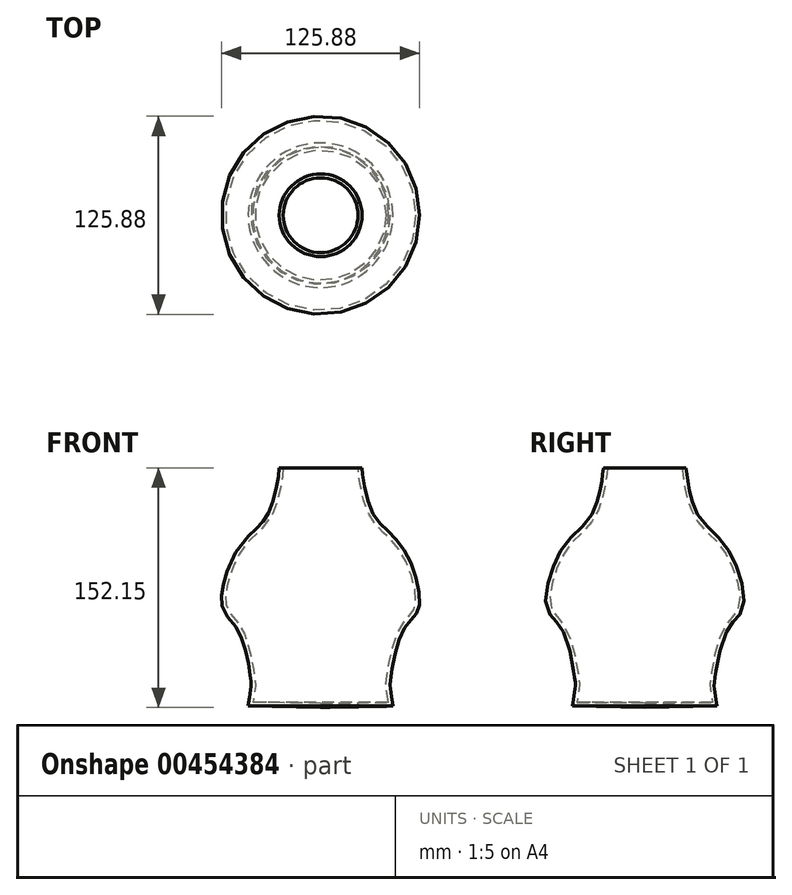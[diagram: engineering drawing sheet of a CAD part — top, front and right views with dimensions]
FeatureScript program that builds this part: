
annotation { "Feature Type Name" : "Feature", "Feature Type Description" : "" }
export const myFeature = defineFeature(function(context is Context, id is Id, definition is map)
    precondition{}
    {
        {
            var Q0;
            Q0=qCreatedBy(makeId("Front.planeOp"),FACE);
            var sketch = newSketch(context, id + "F0", { "sketchPlane" : qUnion([Q0])});
            skFitSpline(sketch, "E0", {"points": [v(45.96, -75.44) * mm, v(44.06, -62.74) * mm, v(44.06, -61.04) * mm, v(52.1, -27.81) * mm, v(62.47, -12.58) * mm, v(51.26, 26.37) * mm, v(32.84, 47.75) * mm, v(26.28, 75.9) * mm, v(26.28, 76.32) * mm], "startDerivative": vector(-22.83, 149.94) * mm, "endDerivative": vector(1.2, 11.01) * mm});
            skLineSegment(sketch, "E1", {"start": v(26.28, 75.9) * mm, "end": v(0, 75.9) * mm});
            skLineSegment(sketch, "E2", {"start": v(0, 75.9) * mm, "end": v(0, -76.25) * mm});
            skLineSegment(sketch, "E3", {"start": v(0, -76.25) * mm, "end": v(45.96, -75.44) * mm});
            skSolve(sketch);
        }
        {
            var Q0;
            Q0 = qSketchRegion(id + "F0", true);
            var Q1;
            Q1=sQuery(id+"F0.wireOp",EDGE,"E2");
            revolve(context, id + "F1", {"entities" : qUnion([Q0]), "axis" : qUnion([Q1]), "revolveType" : RevolveType.FULL});
        }
        {
            var Q0;
            Q0=makeQuery(id+"F1.opRevolve","SWEPT_FACE",FACE,{"disambiguationData":[OSD([sQuery(id+"F0.wireOp",EDGE,"E1")])]});
            shell(context, id + "F2", {"entities" : qUnion([Q0]), "thickness" : 2.54 * mm});
        }
    });
